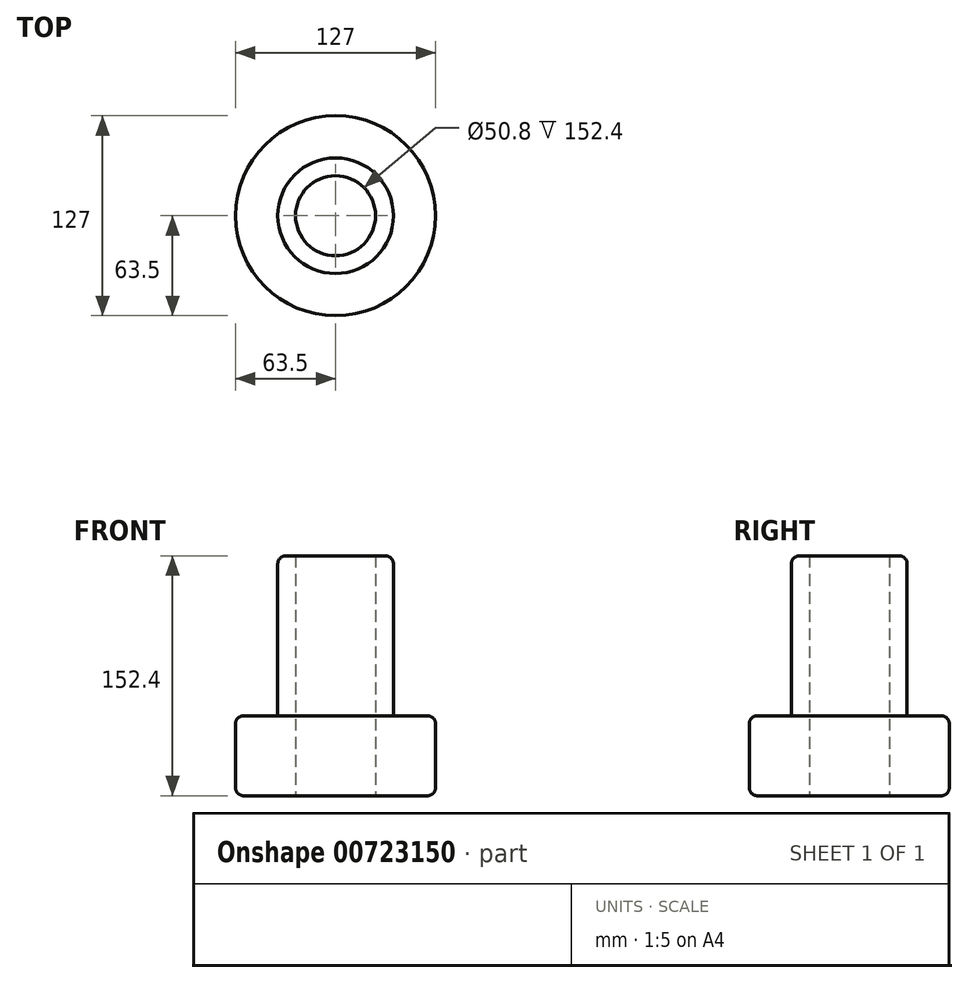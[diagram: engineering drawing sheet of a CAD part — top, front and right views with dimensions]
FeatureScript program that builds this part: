
annotation { "Feature Type Name" : "Feature", "Feature Type Description" : "" }
export const myFeature = defineFeature(function(context is Context, id is Id, definition is map)
    precondition{}
    {
        {
            var Q0;
            Q0=qCreatedBy(makeId("Top.planeOp"),FACE);
            var sketch = newSketch(context, id + "F0", { "sketchPlane" : qUnion([Q0])});
            skCircle(sketch, "E0", {"center": v(0, 0) * mm, "radius": 63.5 * mm});
            skCircle(sketch, "E1", {"center": v(0, 0) * mm, "radius": 36.72 * mm});
            skSolve(sketch);
        }
        {
            var Q0;
            Q0=makeQuery(id+"F0.imprint","IMPRINT",FACE,{"disambiguationData":[TD([[makeQuery(id+"F0.imprint","IMPRINT",EDGE,{"derivedFrom":sQuery(id+"F0.wireOp",EDGE,"E1")}),1.0]])]});
            extrude(context, id + "F1", {"entities" : qUnion([Q0]), "depth" : 101.6 * mm, "offsetDistance" : 25.4 * mm});
        }
        {
            var Q0;
            Q0 = qSketchRegion(id + "F0", true);
            var Q1;
            Q1=makeQuery(id+"F0.imprint","IMPRINT",FACE,{"disambiguationData":[TD([[makeQuery(id+"F0.imprint","IMPRINT",EDGE,{"derivedFrom":sQuery(id+"F0.wireOp",EDGE,"E1")}),1.0]])]});
            extrude(context, id + "F2", {"entities" : qUnion([Q0, Q1]), "operationType" : NewBodyOperationType.ADD, "oppositeDirection" : true, "depth" : 50.8 * mm, "offsetDistance" : 25.4 * mm});
        }
        {
            var Q0;
            Q0=makeQuery(id+"F2.opExtrude","CAP_EDGE",EDGE,{"disambiguationData":[OSD([sQuery(id+"F0.wireOp",EDGE,"E0")])],"isStart":true});
            var Q1;
            Q1=makeQuery(id+"F2.opExtrude","CAP_EDGE",EDGE,{"disambiguationData":[OSD([sQuery(id+"F0.wireOp",EDGE,"E0")])],"isStart":false});
            var Q2;
            Q2=makeQuery(id+"F1.opExtrude","CAP_EDGE",EDGE,{"disambiguationData":[OSD([sQuery(id+"F0.wireOp",EDGE,"E1")])],"isStart":false});
            fillet(context, id + "F3", {"entities" : qUnion([Q0, Q1, Q2]), "radius" : 5.08 * mm, "tangentPropagation" : true, "allowEdgeOverflow" : false});
        }
        {
            var Q0;
            Q0=makeQuery(id+"F2.opExtrude","CAP_FACE",FACE,{"disambiguationData":[OSD([sQuery(id+"F0.wireOp",EDGE,"E0")])],"isStart":false});
            var sketch = newSketch(context, id + "F4", { "sketchPlane" : qUnion([Q0])});
            skCircle(sketch, "E2", {"center": v(0, 0) * mm, "radius": 25.4 * mm});
            skSolve(sketch);
        }
        {
            var Q0;
            Q0 = qSketchRegion(id + "F4", true);
            extrude(context, id + "F5", {"entities" : qUnion([Q0]), "operationType" : NewBodyOperationType.REMOVE, "oppositeDirection" : true, "depth" : 152.4 * mm, "offsetDistance" : 25.4 * mm});
        }
    });
